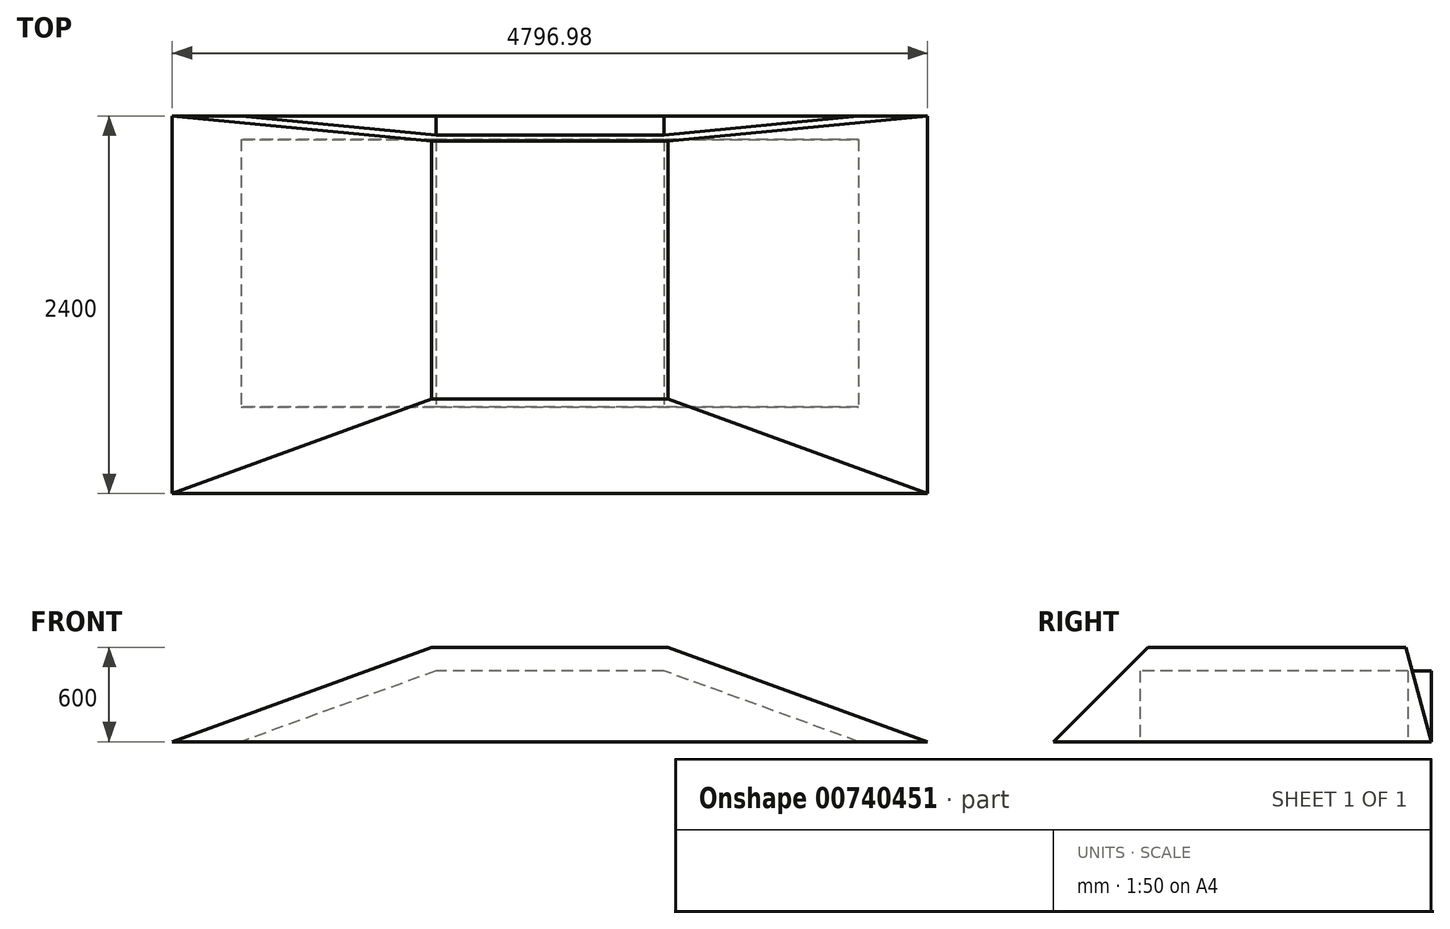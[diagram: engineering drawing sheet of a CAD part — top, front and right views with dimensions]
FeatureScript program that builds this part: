
annotation { "Feature Type Name" : "Feature", "Feature Type Description" : "" }
export const myFeature = defineFeature(function(context is Context, id is Id, definition is map)
    precondition{}
    {
        {
            var Q0;
            Q0=qCreatedBy(makeId("Front.planeOp"),FACE);
            var sketch = newSketch(context, id + "F0", { "sketchPlane" : qUnion([Q0])});
            skLineSegment(sketch, "E0", {"start": v(-2398.49, 0) * mm, "end": v(2398.49, 0) * mm});
            skLineSegment(sketch, "E1", {"start": v(0, 1221.1) * mm, "end": v(0, -343.2) * mm, "construction": true});
            skLineSegment(sketch, "E2", {"start": v(-2398.49, 0) * mm, "end": v(-750, 600) * mm});
            skLineSegment(sketch, "E3", {"start": v(-750, 600) * mm, "end": v(750, 600) * mm});
            skLineSegment(sketch, "E4", {"start": v(750, 600) * mm, "end": v(2398.49, 0) * mm});
            skLineSegment(sketch, "E5", {"start": v(1574.24, 300) * mm, "end": v(497.4, 1054.02) * mm});
            skLineSegment(sketch, "E6", {"start": v(497.4, 1054.02) * mm, "end": v(-750, 600) * mm});
            skLineSegment(sketch, "E7", {"start": v(1959.92, 0) * mm, "end": v(723.55, 450) * mm});
            skLineSegment(sketch, "E8", {"start": v(723.55, 450) * mm, "end": v(-723.55, 450) * mm});
            skLineSegment(sketch, "E9", {"start": v(-723.55, 450) * mm, "end": v(-1959.92, 0) * mm});
            skSolve(sketch);
        }
        {
            var Q0;
            {var subQ0=sQuery(id+"F0.wireOp",EDGE,"E7");Q0=makeQuery(id+"F0.imprint","IMPRINT",FACE,{"disambiguationData":[TD([[makeQuery(id+"F0.imprint","IMPRINT",EDGE,{"derivedFrom":subQ0}),1.0]])]});}
            var Q1;
            {var subQ1=sQuery(id+"F0.wireOp",EDGE,"E2");Q1=makeQuery(id+"F0.imprint","IMPRINT",FACE,{"disambiguationData":[TD([[makeQuery(id+"F0.imprint","IMPRINT",EDGE,{"derivedFrom":subQ1}),-1.0]])]});}
            extrude(context, id + "F1", {"entities" : qUnion([Q0, Q1]), "depth" : 2400 * mm, "offsetDistance" : 25 * mm});
        }
        {
            var Q0;
            Q0=qCreatedBy(makeId("Right.planeOp"),FACE);
            var sketch = newSketch(context, id + "F2", { "sketchPlane" : qUnion([Q0])});
            skPoint(sketch, "E10.0", {"position": v(-2400, 0) * mm});
            skPoint(sketch, "E11.0", {"position": v(-2400, 600) * mm});
            skLineSegment(sketch, "E12", {"start": v(-2400, 0) * mm, "end": v(-1800, 600) * mm});
            skLineSegment(sketch, "E13", {"start": v(-1800, 600) * mm, "end": v(-2400, 600) * mm});
            skLineSegment(sketch, "E14", {"start": v(-2400, 600) * mm, "end": v(-2400, 0) * mm});
            skPoint(sketch, "E15.0", {"position": v(0, 600) * mm});
            skPoint(sketch, "E16.0", {"position": v(0, 0) * mm});
            skLineSegment(sketch, "E17", {"start": v(0, 0) * mm, "end": v(0, 600) * mm});
            skLineSegment(sketch, "E18", {"start": v(-160.77, 600) * mm, "end": v(0, 0) * mm});
            skLineSegment(sketch, "E19", {"start": v(-160.77, 600) * mm, "end": v(0, 600) * mm});
            skSolve(sketch);
        }
        {
            var Q0;
            Q0 = qSketchRegion(id + "F2", true);
            extrude(context, id + "F3", {"entities" : qUnion([Q0]), "operationType" : NewBodyOperationType.REMOVE, "endBound" : BoundingType.THROUGH_ALL, "depth" : 25 * mm, "offsetDistance" : 25 * mm, "hasSecondDirection" : true, "secondDirectionBound" : BoundingType.THROUGH_ALL, "secondDirectionOppositeDirection" : true, "secondDirectionDepth" : 25 * mm});
        }
        {
            var Q0;
            {var subQ0=sQuery(id+"F0.wireOp",EDGE,"E7");Q0=makeQuery(id+"F0.imprint","IMPRINT",FACE,{"disambiguationData":[TD([[makeQuery(id+"F0.imprint","IMPRINT",EDGE,{"derivedFrom":subQ0}),1.0]])]});}
            extrude(context, id + "F4", {"entities" : qUnion([Q0]), "operationType" : NewBodyOperationType.REMOVE, "oppositeDirection" : true, "depth" : 25 * mm, "offsetDistance" : 25 * mm, "hasSecondDirection" : true, "secondDirectionOppositeDirection" : false, "secondDirectionDepth" : 1850 * mm});
        }
        {
            var Q0;
            {var subQ0=sQuery(id+"F0.wireOp",EDGE,"E7");Q0=makeQuery(id+"F0.imprint","IMPRINT",FACE,{"disambiguationData":[TD([[makeQuery(id+"F0.imprint","IMPRINT",EDGE,{"derivedFrom":subQ0}),1.0]])]});}
            extrude(context, id + "F5", {"entities" : qUnion([Q0]), "operationType" : NewBodyOperationType.ADD, "depth" : 150 * mm, "offsetDistance" : 25 * mm});
        }
    });
